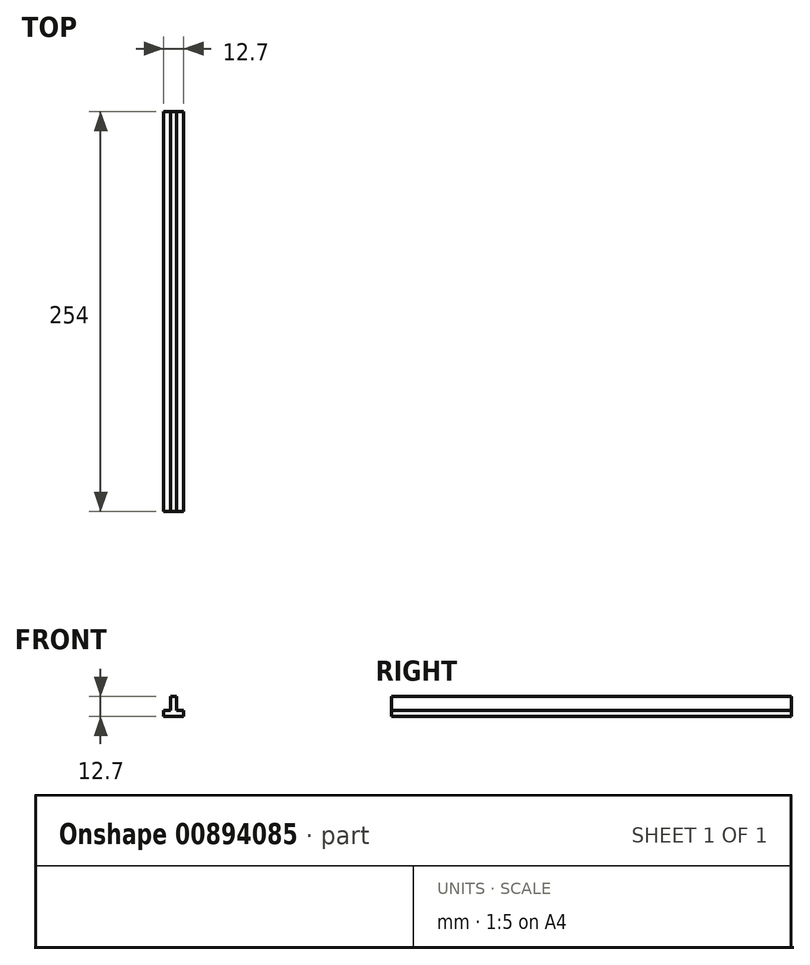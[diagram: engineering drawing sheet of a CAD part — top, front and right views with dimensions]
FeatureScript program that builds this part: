
annotation { "Feature Type Name" : "Feature", "Feature Type Description" : "" }
export const myFeature = defineFeature(function(context is Context, id is Id, definition is map)
    precondition{}
    {
        {
            var Q0;
            Q0=qCreatedBy(makeId("Front.planeOp"),FACE);
            var sketch = newSketch(context, id + "F0", { "sketchPlane" : qUnion([Q0])});
            skLineSegment(sketch, "E0.bottom", {"start": v(-1.9, 8.9) * mm, "end": v(1.9, 8.9) * mm});
            skLineSegment(sketch, "E0.top", {"start": v(-1.9, 0) * mm, "end": v(1.9, 0) * mm});
            skLineSegment(sketch, "E0.left", {"start": v(-1.9, 8.9) * mm, "end": v(-1.9, 0) * mm});
            skLineSegment(sketch, "E0.right", {"start": v(1.9, 8.9) * mm, "end": v(1.9, 0) * mm});
            skLineSegment(sketch, "E1.bottom", {"start": v(-6.35, 0) * mm, "end": v(6.35, 0) * mm});
            skLineSegment(sketch, "E1.top", {"start": v(-6.35, -3.8) * mm, "end": v(6.35, -3.8) * mm});
            skLineSegment(sketch, "E1.left", {"start": v(-6.35, 0) * mm, "end": v(-6.35, -3.8) * mm});
            skLineSegment(sketch, "E1.right", {"start": v(6.35, 0) * mm, "end": v(6.35, -3.8) * mm});
            skSolve(sketch);
        }
        {
            var Q0;
            Q0=makeQuery(id+"F0.imprint","IMPRINT",FACE,{"disambiguationData":[TD([[makeQuery(id+"F0.imprint","IMPRINT",EDGE,{"derivedFrom":sQuery(id+"F0.wireOp",EDGE,"E1.top")}),1.0]])]});
            var Q1;
            Q1=makeQuery(id+"F0.imprint","IMPRINT",FACE,{"disambiguationData":[TD([[makeQuery(id+"F0.imprint","IMPRINT",EDGE,{"derivedFrom":sQuery(id+"F0.wireOp",EDGE,"E0.bottom")}),-1.0]])]});
            extrude(context, id + "F1", {"entities" : qUnion([Q0, Q1]), "depth" : 254 * mm, "offsetDistance" : 25.4 * mm});
        }
    });
